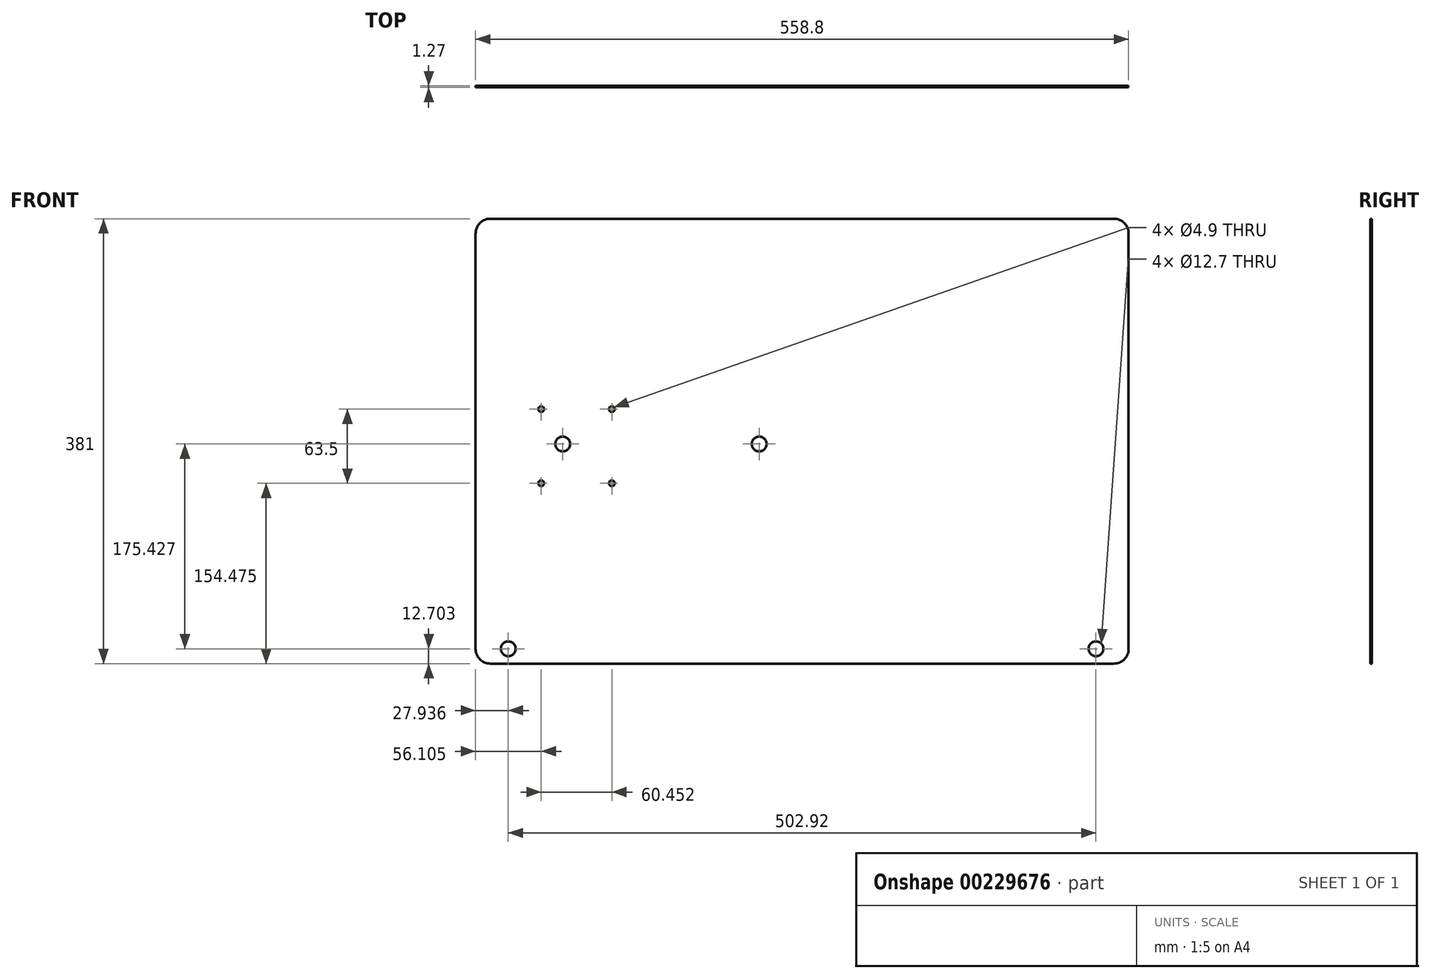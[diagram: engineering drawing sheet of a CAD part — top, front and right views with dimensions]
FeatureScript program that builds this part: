
annotation { "Feature Type Name" : "Feature", "Feature Type Description" : "" }
export const myFeature = defineFeature(function(context is Context, id is Id, definition is map)
    precondition{}
    {
        {
            var Q0;
            Q0=qCreatedBy(makeId("Front.planeOp"),FACE);
            var sketch = newSketch(context, id + "F0", { "sketchPlane" : qUnion([Q0])});
            skLineSegment(sketch, "E0", {"start": v(-74.52, 180.17) * mm, "end": v(-74.52, -175.43) * mm});
            skLineSegment(sketch, "E1", {"start": v(-61.82, 192.87) * mm, "end": v(471.58, 192.87) * mm});
            skLineSegment(sketch, "E2", {"start": v(484.28, 180.17) * mm, "end": v(484.28, -175.43) * mm});
            skLineSegment(sketch, "E3", {"start": v(-61.82, -188.13) * mm, "end": v(471.58, -188.13) * mm});
            skPoint(sketch, "E4.visualSharp", {"position": v(-74.52, 192.87) * mm});
            skArc(sketch, "E4.filletArc", {"start": v(-61.82, 192.87) * mm, "mid": v(-70.8, 189.15) * mm, "end": v(-74.52, 180.17) * mm});
            skPoint(sketch, "E5.visualSharp", {"position": v(-74.52, -188.13) * mm});
            skArc(sketch, "E5.filletArc", {"start": v(-74.52, -175.43) * mm, "mid": v(-70.8, -184.4) * mm, "end": v(-61.82, -188.13) * mm});
            skPoint(sketch, "E6.visualSharp", {"position": v(484.28, -188.13) * mm});
            skArc(sketch, "E6.filletArc", {"start": v(471.58, -188.13) * mm, "mid": v(480.56, -184.4) * mm, "end": v(484.28, -175.43) * mm});
            skPoint(sketch, "E7.visualSharp", {"position": v(484.28, 192.87) * mm});
            skArc(sketch, "E7.filletArc", {"start": v(484.28, 180.17) * mm, "mid": v(480.56, 189.15) * mm, "end": v(471.58, 192.87) * mm});
            skLineSegment(sketch, "E8", {"start": v(-23.11, 36.2) * mm, "end": v(-23.11, -40) * mm, "construction": true});
            skLineSegment(sketch, "E9", {"start": v(-23.11, -40) * mm, "end": v(46.74, -40) * mm, "construction": true});
            skLineSegment(sketch, "E10", {"start": v(46.74, -40) * mm, "end": v(46.74, 36.2) * mm, "construction": true});
            skPoint(sketch, "E11", {"position": v(0, 0) * mm});
            skLineSegment(sketch, "E12", {"start": v(-23.11, 36.2) * mm, "end": v(46.74, 36.2) * mm, "construction": true});
            skPoint(sketch, "E13", {"position": v(-18.42, 29.85) * mm});
            skPoint(sketch, "E14", {"position": v(42.04, 29.85) * mm});
            skPoint(sketch, "E15", {"position": v(42.04, -33.66) * mm});
            skPoint(sketch, "E16", {"position": v(-18.42, -33.66) * mm});
            skCircle(sketch, "E17", {"center": v(-18.42, 29.85) * mm, "radius": 2.45 * mm});
            skCircle(sketch, "E18", {"center": v(42.04, 29.85) * mm, "radius": 2.45 * mm});
            skCircle(sketch, "E19", {"center": v(42.04, -33.66) * mm, "radius": 2.45 * mm});
            skCircle(sketch, "E20", {"center": v(-18.42, -33.66) * mm, "radius": 2.45 * mm});
            skCircle(sketch, "E21", {"center": v(0, 0) * mm, "radius": 6.35 * mm});
            skLineSegment(sketch, "E22", {"start": v(0, 0) * mm, "end": v(168.15, 0) * mm, "construction": true});
            skCircle(sketch, "E23", {"center": v(168.15, 0) * mm, "radius": 6.35 * mm});
            skLineSegment(sketch, "E24", {"start": v(-74.52, -175.43) * mm, "end": v(-46.58, -175.43) * mm, "construction": true});
            skPoint(sketch, "E25", {"position": v(-46.58, -175.43) * mm});
            skCircle(sketch, "E26", {"center": v(-46.58, -175.43) * mm, "radius": 6.35 * mm});
            skLineSegment(sketch, "E27", {"start": v(204.88, 192.87) * mm, "end": v(204.88, -188.13) * mm, "construction": true});
            skCircle(sketch, "E28.MirrorC", {"center": v(456.34, -175.43) * mm, "radius": 6.35 * mm});
            skSolve(sketch);
        }
        {
            var Q0;
            Q0 = qSketchRegion(id + "F0", true);
            extrude(context, id + "F1", {"entities" : qUnion([Q0]), "depth" : 1.27 * mm});
        }
    });
